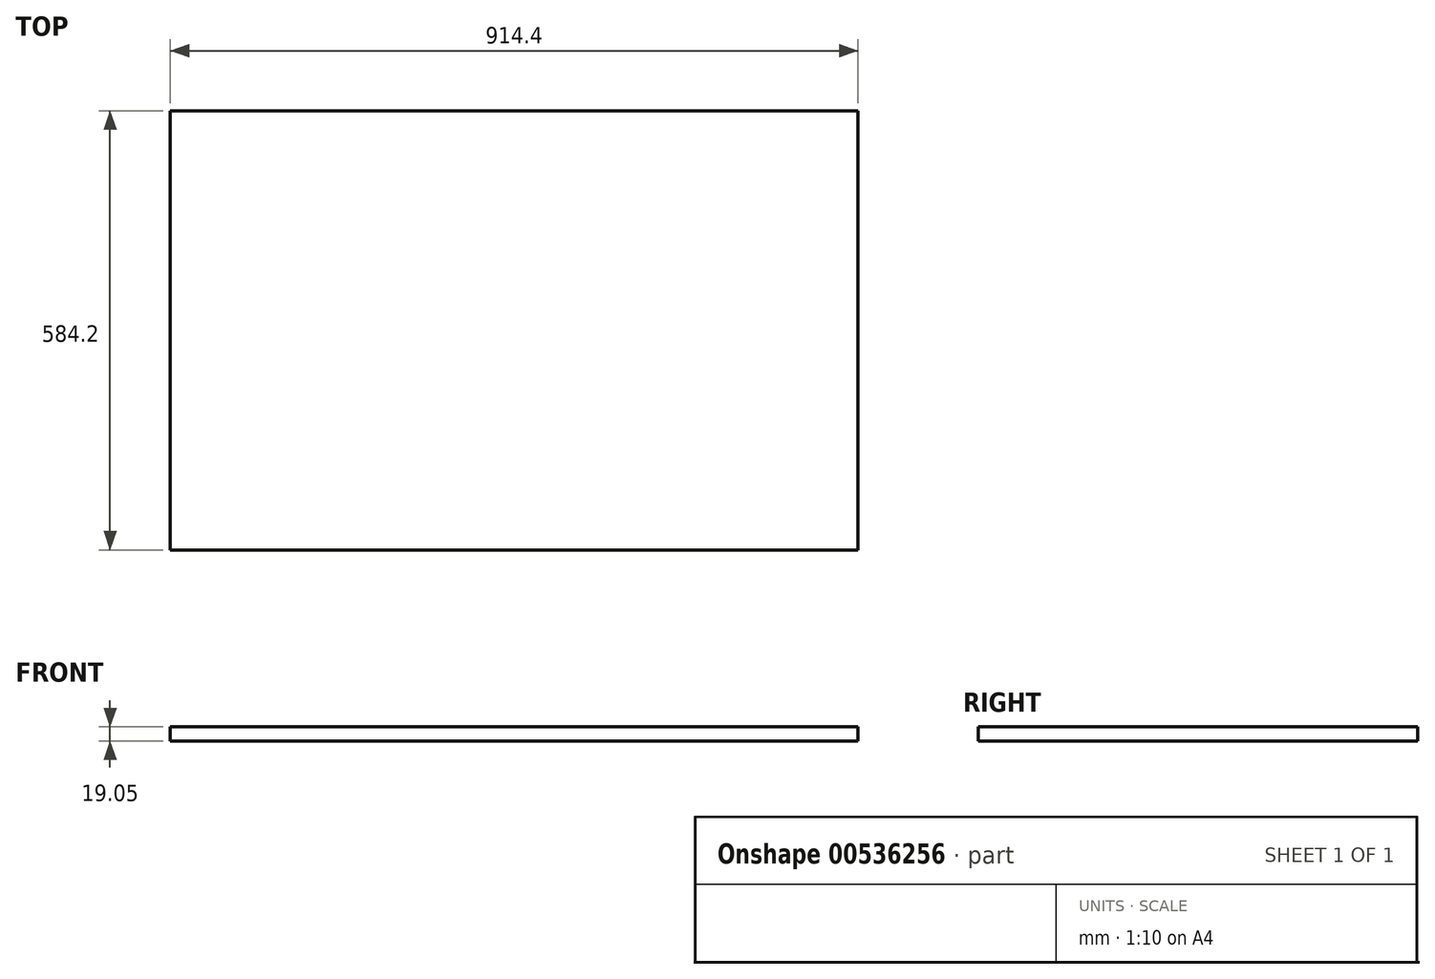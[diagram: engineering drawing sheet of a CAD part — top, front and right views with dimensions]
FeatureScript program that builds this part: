
annotation { "Feature Type Name" : "Feature", "Feature Type Description" : "" }
export const myFeature = defineFeature(function(context is Context, id is Id, definition is map)
    precondition{}
    {
        {
            var Q0;
            Q0=qCreatedBy(makeId("Top.planeOp"),FACE);
            var sketch = newSketch(context, id + "F0", { "sketchPlane" : qUnion([Q0])});
            skLineSegment(sketch, "E0.bottom", {"start": v(457.2, 292.1) * mm, "end": v(-457.2, 292.1) * mm});
            skLineSegment(sketch, "E0.top", {"start": v(457.2, -292.1) * mm, "end": v(-457.2, -292.1) * mm});
            skLineSegment(sketch, "E0.left", {"start": v(457.2, 292.1) * mm, "end": v(457.2, -292.1) * mm});
            skLineSegment(sketch, "E0.right", {"start": v(-457.2, 292.1) * mm, "end": v(-457.2, -292.1) * mm});
            skPoint(sketch, "E0.middle", {"position": v(0, 0) * mm});
            skSolve(sketch);
        }
        {
            var Q0;
            Q0 = qSketchRegion(id + "F0", true);
            extrude(context, id + "F1", {"entities" : qUnion([Q0]), "depth" : 19.05 * mm, "offsetDistance" : 25.4 * mm});
        }
    });
